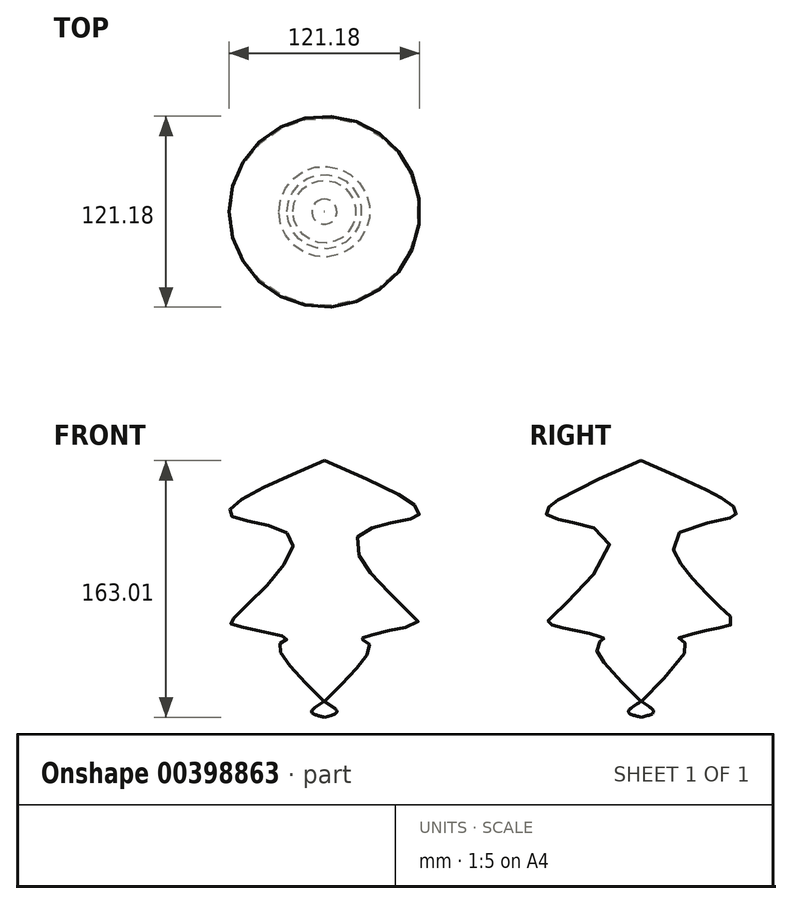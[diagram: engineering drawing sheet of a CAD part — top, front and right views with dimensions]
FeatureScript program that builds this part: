
annotation { "Feature Type Name" : "Feature", "Feature Type Description" : "" }
export const myFeature = defineFeature(function(context is Context, id is Id, definition is map)
    precondition{}
    {
        {
            var Q0;
            Q0=qCreatedBy(makeId("Front.planeOp"),FACE);
            var sketch = newSketch(context, id + "F0", { "sketchPlane" : qUnion([Q0])});
            skLineSegment(sketch, "E0", {"start": v(0, -76.37) * mm, "end": v(0, 76.8) * mm});
            skFitSpline(sketch, "E1", {"points": [v(0, -76.37) * mm, v(-28.26, -39.54) * mm, v(-23.68, -36.25) * mm, v(-58.6, -27.1) * mm, v(-59, -24.85) * mm, v(-20.25, 26.29) * mm, v(-59.62, 42) * mm, v(0, 76.8) * mm], "startDerivative": vector(-278.89, 274.9) * mm, "endDerivative": vector(476.52, 204.51) * mm});
            skSolve(sketch);
        }
        {
            var Q0;
            Q0=makeQuery(id+"F0.imprint","IMPRINT",FACE,{"disambiguationData":[TD([[makeQuery(id+"F0.imprint","IMPRINT",EDGE,{"derivedFrom":sQuery(id+"F0.wireOp",EDGE,"E0")}),1.0]])]});
            var Q1;
            Q1=sQuery(id+"F0.wireOp",EDGE,"E0");
            revolve(context, id + "F1", {"entities" : qUnion([Q0]), "axis" : qUnion([Q1]), "revolveType" : RevolveType.FULL, "oppositeDirection" : true});
        }
        {
            var Q0;
            Q0=qCreatedBy(makeId("Right.planeOp"),FACE);
            var sketch = newSketch(context, id + "F2", { "sketchPlane" : qUnion([Q0])});
            skLineSegment(sketch, "E2", {"start": v(0, -76.27) * mm, "end": v(0, -86.21) * mm});
            skFitSpline(sketch, "E3", {"points": [v(0, -86.21) * mm, v(7.99, -82.83) * mm, v(0, -76.27) * mm], "startDerivative": vector(24.36, 5.77) * mm, "endDerivative": vector(-23.66, 14) * mm});
            skSolve(sketch);
        }
        {
            var Q0;
            Q0=makeQuery(id+"F2.imprint","IMPRINT",FACE,{"disambiguationData":[TD([[makeQuery(id+"F2.imprint","IMPRINT",EDGE,{"derivedFrom":sQuery(id+"F2.wireOp",EDGE,"E2")}),1.0]])]});
            var Q1;
            Q1=sQuery(id+"F2.wireOp",EDGE,"E2");
            revolve(context, id + "F3", {"operationType" : NewBodyOperationType.ADD, "entities" : qUnion([Q0]), "axis" : qUnion([Q1]), "revolveType" : RevolveType.FULL});
        }
    });
